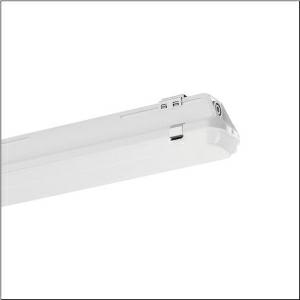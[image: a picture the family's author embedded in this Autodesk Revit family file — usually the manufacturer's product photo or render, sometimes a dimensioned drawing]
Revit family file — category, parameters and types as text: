
# Revit family: monsun_21_51fb207l420k
name_source: partatom
category: Lighting Fixtures
units: mm (PartAtom-declared; Revit-internal decimal feet)

## family parameters
Cut with Voids When Loaded = No
Host = Face
Light Source = No
Part Type = Normal
Room Calculation Point = No
Round Connector Dimension = Use Diameter
Shared = No

## types (1)
- Monsun 21 (1 x LED, 2620 lm, 17.1 W, 4000K)
    Apparent Load = 17 VA
    CIE Flux Codes = 45 75 93 94 100
    Color Rendering = 80
    Color Temperature = 4000K
    Default Elevation = 1800 mm
    Description = Monsun 21, damp-proof luminaire, chain hanger, primary optical cover: enclosure, of PC, light emission: direct distribution, primary light characteristic: symmetric, installation type: suspended mounting, surface-mounted, horizontal mounting, vertical mounting, LED, rated luminous flux: 2.620lm, luminous efficacy: 153lm/W, light colour: 840, colour temperature: 4000K, control gear: ON/OFF, with terminal, 3-pole, max. 2.5mm², mains connection: 220..240V, AC, 50/60Hz, rated input power: 17W, housing, of glass-fibre reinforced plastic, uncoated, bright grey, incl. chain hanger, length: 1.299mm, width: 90mm, height: 88mm, clip for enclosure, of stainless steel (V2A), ceiling mounting element, of stainless steel (V2A), chain hanger, of stainless steel (V2A), protection rating (complete): IP66, insulation class (complete): insulation class I (protective earthing), certification: CE, ENEC, VDE, UKCA, protection symbol: D, impact resistance: IK08, permissible operating ambient temperature: -25..+35°C, standard: EN 50419, EN 60598-2-1, corresponds to IFS (International Featured Standards) requirements for safety and quality in the food industry, for indoor or canopied outdoor use, no direct snow, no direct sun, no direct rain, LABS conformity tested according to VDMA 24364:2018-05, contact your sales advisor before using the luminaires in applications with unclear chemical exposure, large temperature fluctuations or condensation-forming humidity, packaging unit: 1 piece
    Height = 88 mm
    Lamp = 1 x LED
    Lamp Light Flux = 2620 lm
    Lamp Power = 17.1 W
    Lamp count = 1
    Length = 1299 mm
    Luminous efficacy = 153 lm/W
    Manufacturer = Siteco
    ModVariant = No
    Model = 51FB207L420K
    Mounting Place = Ceiling
    Mounting Type = Surface mounted
    Number of Poles = 1
    OnlyDefault = Yes
    Power Factor = 1
    Product Name = Monsun 21
    Product group = damp-proof luminaire
    ProductGroupID = 300
    Protection Class = Protection class I
    Protection Degree = IP 66
    RLX_Detail_Level = 1
    RLX_Emergency_Light_Flux = 0 lm
    RLX_Emergency_Type = 0
    RLX_Emergency_Type_DB = No
    RlxData = <blob elided: 89681 chars, md5=0a674d8c>
    Socket = socket
    Standby Power = 0 W
    System Light Flux = 2620 lm
    System Power = 17 W
    Type Comments = Product without accessories
    Type Image = l_1319656.jpg
    URL = http://relux.com
    VarID = ---
    Voltage = 0 V
    Weight = 0.00 kg
    Width = 90 mm

## geometry (parser evidence)
native form markers: Blend x4, Sweep x13
no freeform markers — native parametric forms only
